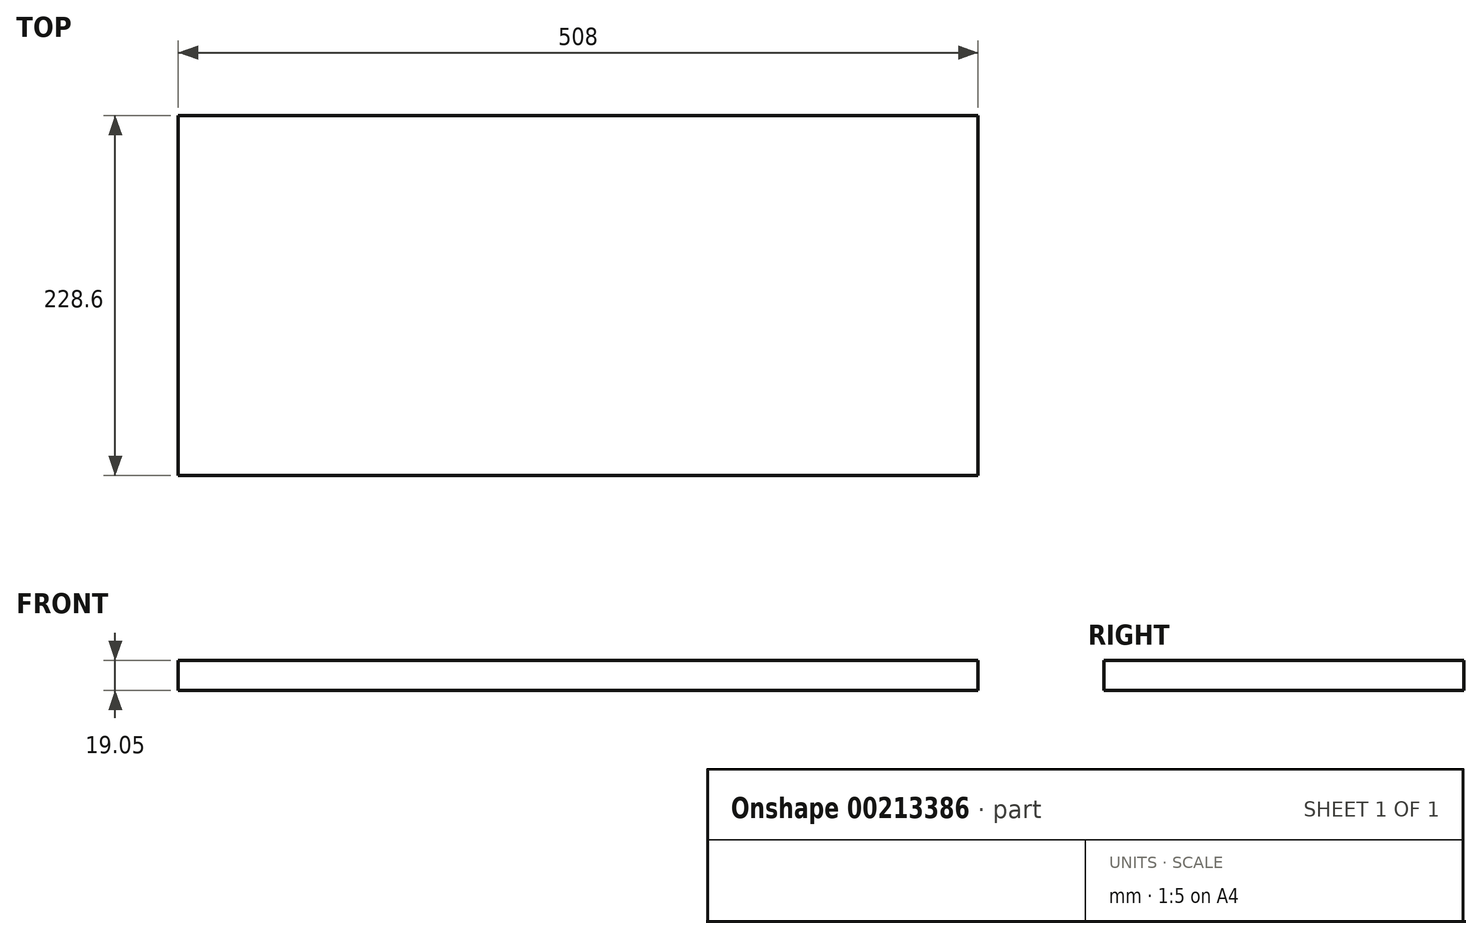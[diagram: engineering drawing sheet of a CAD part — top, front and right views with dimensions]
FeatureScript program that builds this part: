
annotation { "Feature Type Name" : "Feature", "Feature Type Description" : "" }
export const myFeature = defineFeature(function(context is Context, id is Id, definition is map)
    precondition{}
    {
        {
            var Q0;
            Q0=qCreatedBy(makeId("Top.planeOp"),FACE);
            var sketch = newSketch(context, id + "F0", { "sketchPlane" : qUnion([Q0])});
            skLineSegment(sketch, "E0.bottom", {"start": v(254, 114.3) * mm, "end": v(-254, 114.3) * mm});
            skLineSegment(sketch, "E0.top", {"start": v(254, -114.3) * mm, "end": v(-254, -114.3) * mm});
            skLineSegment(sketch, "E0.left", {"start": v(254, 114.3) * mm, "end": v(254, -114.3) * mm});
            skLineSegment(sketch, "E0.right", {"start": v(-254, 114.3) * mm, "end": v(-254, -114.3) * mm});
            skPoint(sketch, "E0.middle", {"position": v(0, 0) * mm});
            skSolve(sketch);
        }
        {
            var Q0;
            Q0=makeQuery(id+"F0.imprint","IMPRINT",FACE,{"disambiguationData":[TD([[makeQuery(id+"F0.imprint","IMPRINT",EDGE,{"derivedFrom":sQuery(id+"F0.wireOp",EDGE,"E0.bottom")}),1.0]])]});
            extrude(context, id + "F1", {"entities" : qUnion([Q0]), "depth" : 19.05 * mm});
        }
    });
